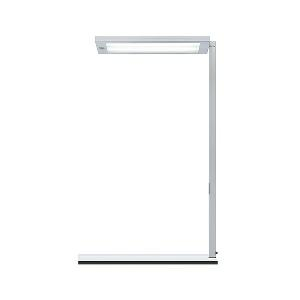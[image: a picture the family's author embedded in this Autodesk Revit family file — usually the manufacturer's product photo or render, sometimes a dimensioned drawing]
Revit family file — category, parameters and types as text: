
# Revit family: lavigo_-_dpt_14000_840_r_g2_00804502_4c24
name_source: partatom
category: Lighting Fixtures
units: mm (PartAtom-declared; Revit-internal decimal feet)

## family parameters
Cut with Voids When Loaded = No
Host = Face
Light Source = No
Part Type = Normal
Room Calculation Point = No
Round Connector Dimension = Use Diameter
Shared = No

## types (1)
- LAVIGO - DPT 14000/840/R/G2 (1 x LED, 14050 lm, 4000K)
    Apparent Load = 93 VA
    Approval mark = CE
    CIE Flux Codes = 60 87 97 12 100
    Color Rendering = 80-89
    Color Temperature = 4000K
    Control Gear = Electronic ballast
    Default Elevation = 1800 mm
    Description = DPT 14000/840/R/G2|Desk-mounted luminaire|light source: LED|work equipment: Electronic ballast|connected load: 220-240 V, 50/60 Hz|Power consumption: approx. 93 W|standby: approx. 0,50|power factor: approx. 0,943|luminous flux: 14050 lm|luminous efficacy: 151 lm/W|light distribution: Direct/indirect|direct ratio: approx. 12 %|colour temperature: Cold white, ca. 4000 K|color rendering index (CRI): >= 80|chromaticity tolerance:  3 SDCM|technology: Presence and daylight sensor control (PIR)|operation: Multi-function switch|luminaire body|material: Steel/plastic|surface: Painted|colour: White|lamp cover: Acrylic (PMMA), Satine|tubular section|material: Steel tube|surface: Painted|Form: Tubular section upright|colour of tubular section: White|weight (net): approx. 9.5 kg|mains lead: 3.70 m Mains plug CEE 7/VII|Fastening: Socket, Table adaptor|decorative contrast side parts: Flint grey|glare control: Prism aperture|luminance(L65): <= 3000 cd/m|unified glare rating(4H 8H): <=  16|special features: Luminaire head detachable, Cradle to Cradle Certified TM, Direct light component with edge light and light-guide technology for homogenous light exit, Flicker-free, Integrated light and presence sensor PIR, Retrofittable with TALK module, Inclination of tubular section adjustable, Separated, direct and indirect light individually adjustable|Approval mark: VDE - ENEC|
    Frequency = 50 Hz, 60 Hz
    Height = 36 mm
    Lamp = 1 x LED
    Lamp Light Flux = 14050 lm
    Lamp count = 1
    Length = 675 mm
    Luminous efficacy = 151 lm/W
    Manufacturer = Waldmann
    ModVariant = No
    Model = 00804502
    Mounting Place = Table
    Mounting Type = Surface mounted
    Number of Poles = 1
    OnlyDefault = Yes
    Power Factor = 1
    Product Name = LAVIGO - DPT 14000/840/R/G2
    Product group = Desk mounted luminaire with detector
    ProductGroupID = 2201
    Protection Class = Protection class I
    Protection Degree = IP 20
    RLX_Detail_Level = 1
    RLX_Emergency_Light_Flux = 0 lm
    RLX_Emergency_Type = 0
    RLX_Emergency_Type_DB = No
    RlxData = <blob elided: 35221 chars, md5=e7059d87>
    Socket = socket
    Standby Power = 0 W
    System Light Flux = 14050 lm
    System Power = 93 W
    Type Comments = Product without accessories
    Type Image = 121716000-00630762.jpg
    URL = http://relux.com
    VarID = ---
    Voltage = 230 V
    Voltage Range = 220-240 V
    Weight = 0.00 kg
    Width = 320 mm

## geometry (parser evidence)
native form markers: Blend x4, Sweep x16
no freeform markers — native parametric forms only
